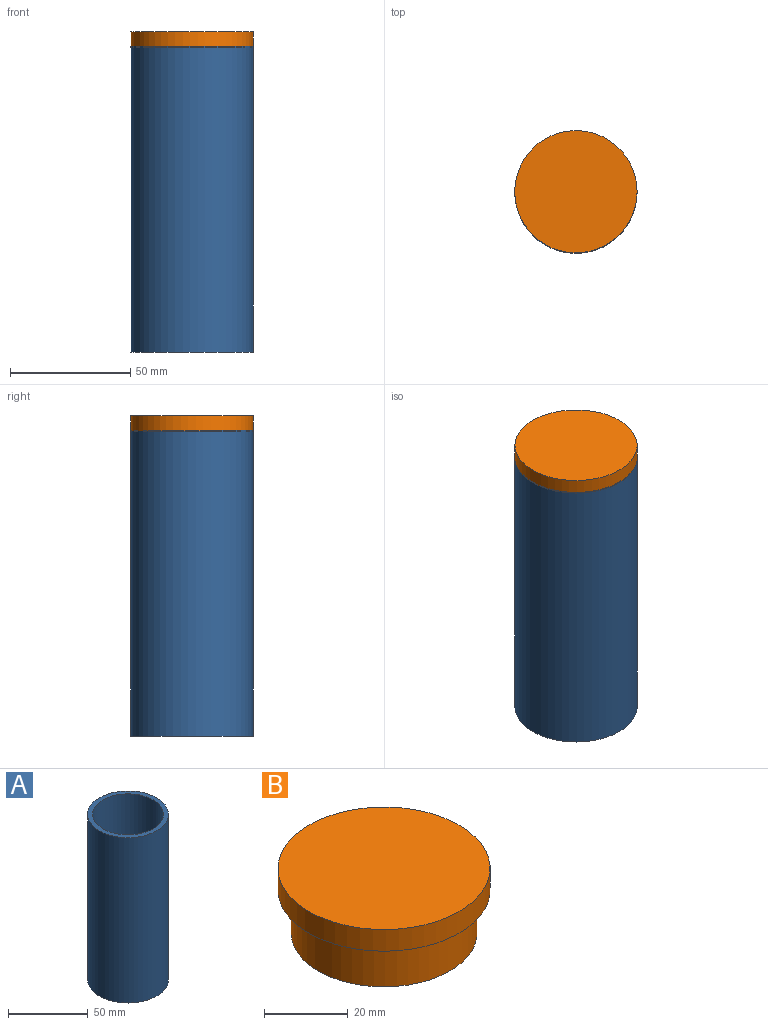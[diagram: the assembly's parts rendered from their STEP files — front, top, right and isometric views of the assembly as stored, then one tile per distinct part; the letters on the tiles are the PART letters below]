
ASSEMBLY  parts=2 mates=1
PART A: 5 faces, bbox 50.8x50.8x127 mm
  f0: cylinder r=25.4mm len=127mm, axis (0,0,-1), area 20268.3mm2, adj f1,f2
  f1: plane 50.8x50.8mm, normal (0,0,1), area 475mm2, adj f0,f3
  f2: plane 50.8x50.8mm, normal (0,0,-1), area 2026.8mm2, adj f0
  f3: cylinder r=22.23mm len=101.6mm, axis (0,0,1), area 14187.8mm2, adj f1,f4
  f4: plane 44.45x44.45mm, normal (0,0,1), area 1551.8mm2, adj f3
PART B: 5 faces, bbox 50.8x50.8x19.1 mm
  f0: cylinder r=25.4mm len=50.8mm, axis (0,0,-1), area 1013.4mm2, adj f1,f2
  f1: plane 50.8x50.8mm, normal (0,0,1), area 2026.8mm2, adj f0
  f2: plane 50.8x50.8mm, normal (0,0,-1), area 475mm2, adj f0,f3
  f3: cylinder r=22.23mm len=44.45mm, axis (0,0,1), area 1773.5mm2, adj f2,f4
  f4: plane 44.45x44.45mm, normal (0,0,-1), area 1551.8mm2, adj f3
PLACE A t=(-11.82,-1.16,-9.39)mm
PLACE B t=(-36.51,18.33,117.3)mm
MATE cylindrical B.f3 <-> A.f0  axis (0,0,-1) through (-36.51,18.33,104.6)mm
